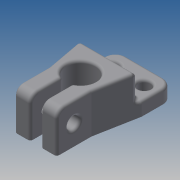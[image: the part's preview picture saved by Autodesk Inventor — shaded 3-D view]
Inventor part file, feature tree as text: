
AUTODESK INVENTOR PART (.ipt)
format: ipt  version: 2014 (Build 180170000, 170)  size: 308,736 bytes
history: native  units: mm
features: fillet x6, extrude x4, sketch x4, chamfer x1
ambient origin geometry x8: Origin, YZ Plane, XZ Plane, XY Plane, X Axis, Y Axis, Z Axis, Center Point
bodies: Solid1 (feature_tree)
feature tree (15):
  extrude  "Extrusion1"  Depth=12.0mm
  extrude  "Extrusion2"  Depth=5.0mm
  extrude  "Extrusion3"  Depth=10.0mm
  extrude  "Extrusion4"  Depth=1.0mm
  chamfer  "Chamfer1"  Distance=12.0mm
  fillet  "Fillet1"  Radius=4.0mm
  fillet  "Fillet2"  Radius=6.0mm
  fillet  "Fillet3"  Radius=16.0mm
  fillet  "Fillet4"  Radius=15.0mm
  fillet  "Fillet5"  Radius=4.5mm
  fillet  "Fillet6"  Radius=25.0mm
  sketch  "Sketch1"  dims[d0=4.6mm d1=12.0mm]
  sketch  "Sketch2"  dims[d2=12.0mm d3=5.0mm]
  sketch  "Sketch3"  dims[d4=5.0mm d5=0.0mm d6=10.0mm]
  sketch  "Sketch4"  dims[d7=18.0mm d8=0.5mm d9=12.0mm d10=4.0mm d11=6.0mm d12=16.0mm d13=15.0mm d14=0.0mm d15=4.5mm d16=25.0mm d17=0.0mm d18=7.3mm d19=3.0mm d20=0.0mm d21=2.5mm d22=2.0mm d23=45.0deg d24=4.0mm d25=1.0mm d26=1.0mm d27=3.0mm d28=1.0mm d29=1.0mm]
